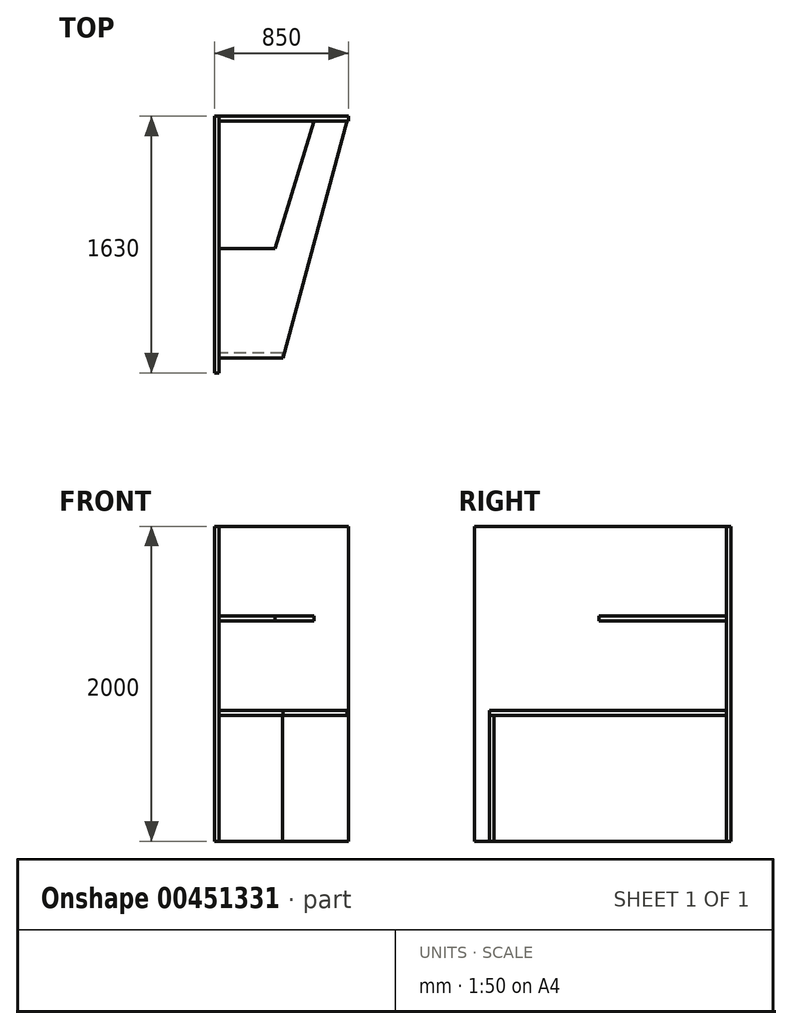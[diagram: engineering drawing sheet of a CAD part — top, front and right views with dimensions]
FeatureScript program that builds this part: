
annotation { "Feature Type Name" : "Feature", "Feature Type Description" : "" }
export const myFeature = defineFeature(function(context is Context, id is Id, definition is map)
    precondition{}
    {
        {
            var Q0;
            Q0=qCreatedBy(makeId("Top.planeOp"),FACE);
            var sketch = newSketch(context, id + "F0", { "sketchPlane" : qUnion([Q0])});
            skLineSegment(sketch, "E0.bottom", {"start": v(0, 0) * mm, "end": v(820, 0) * mm});
            skLineSegment(sketch, "E0.top", {"start": v(0, -30) * mm, "end": v(820, -30) * mm});
            skLineSegment(sketch, "E0.left", {"start": v(0, 0) * mm, "end": v(0, -30) * mm});
            skLineSegment(sketch, "E0.right", {"start": v(820, 0) * mm, "end": v(820, -30) * mm});
            skLineSegment(sketch, "E1.bottom", {"start": v(0, 0) * mm, "end": v(-30, 0) * mm});
            skLineSegment(sketch, "E1.top", {"start": v(0, -1630) * mm, "end": v(-30, -1630) * mm});
            skLineSegment(sketch, "E1.left", {"start": v(0, 0) * mm, "end": v(0, -1630) * mm});
            skLineSegment(sketch, "E1.right", {"start": v(-30, 0) * mm, "end": v(-30, -1630) * mm});
            skSolve(sketch);
        }
        {
            var Q0;
            Q0 = qSketchRegion(id + "F0", true);
            extrude(context, id + "F1", {"entities" : qUnion([Q0]), "depth" : 2000 * mm});
        }
        {
            var Q0;
            Q0=qCreatedBy(makeId("Top.planeOp"),FACE);
            cPlane(context, id + "F2", {"entities" : qUnion([Q0]), "cplaneType" : CPlaneType.OFFSET, "offset" : 800 * mm, "width" : 150 * mm, "height" : 150 * mm});
        }
        {
            var Q0;
            Q0=qCreatedBy(id+"F2.planeOp",FACE);
            var sketch = newSketch(context, id + "F3", { "sketchPlane" : qUnion([Q0])});
            skLineSegment(sketch, "E2", {"start": v(0, -30) * mm, "end": v(810, -30) * mm});
            skLineSegment(sketch, "E3", {"start": v(810, -30) * mm, "end": v(405, -1535) * mm});
            skLineSegment(sketch, "E4", {"start": v(405, -1535) * mm, "end": v(0, -1535) * mm});
            skLineSegment(sketch, "E5", {"start": v(0, -1535) * mm, "end": v(0, -30) * mm});
            skSolve(sketch);
        }
        {
            var Q0;
            Q0=qCreatedBy(makeId("Top.planeOp"),FACE);
            var sketch = newSketch(context, id + "F4", { "sketchPlane" : qUnion([Q0])});
            skSolve(sketch);
        }
        {
            var Q0;
            Q0 = qSketchRegion(id + "F3", true);
            extrude(context, id + "F5", {"entities" : qUnion([Q0]), "depth" : 30 * mm});
        }
        {
            var Q0;
            Q0=qCreatedBy(makeId("Top.planeOp"),FACE);
            cPlane(context, id + "F6", {"entities" : qUnion([Q0]), "cplaneType" : CPlaneType.OFFSET, "offset" : 1400 * mm, "width" : 150 * mm, "height" : 150 * mm});
        }
        {
            var Q0;
            Q0=qCreatedBy(id+"F6.planeOp",FACE);
            var sketch = newSketch(context, id + "F7", { "sketchPlane" : qUnion([Q0])});
            skLineSegment(sketch, "E6", {"start": v(0, -840) * mm, "end": v(355, -840) * mm});
            skLineSegment(sketch, "E7", {"start": v(355, -840) * mm, "end": v(600, -30) * mm});
            skLineSegment(sketch, "E8", {"start": v(600, -30) * mm, "end": v(0, -30) * mm});
            skLineSegment(sketch, "E9", {"start": v(0, -30) * mm, "end": v(0, -840) * mm});
            skSolve(sketch);
        }
        {
            var Q0;
            Q0 = qSketchRegion(id + "F7", true);
            extrude(context, id + "F8", {"entities" : qUnion([Q0]), "operationType" : NewBodyOperationType.ADD, "depth" : 30 * mm});
        }
        {
            var Q0;
            Q0=makeQuery(id+"F1.opExtrude","CAP_FACE",FACE,{"disambiguationData":[OSD([sQuery(id+"F0.wireOp",EDGE,"E1.bottom"),sQuery(id+"F0.wireOp",EDGE,"E1.top"),sQuery(id+"F0.wireOp",EDGE,"E1.left"),sQuery(id+"F0.wireOp",EDGE,"E1.right")])],"isStart":true});
            var sketch = newSketch(context, id + "F9", { "sketchPlane" : qUnion([Q0])});
            skLineSegment(sketch, "E10.bottom", {"start": v(400, 1535) * mm, "end": v(0, 1535) * mm});
            skLineSegment(sketch, "E10.top", {"start": v(400, 1505) * mm, "end": v(0, 1505) * mm});
            skLineSegment(sketch, "E10.left", {"start": v(0, 1535) * mm, "end": v(0, 1505) * mm});
            skLineSegment(sketch, "E10.right", {"start": v(400, 1535) * mm, "end": v(400, 1505) * mm});
            skSolve(sketch);
        }
        {
            var Q0;
            Q0 = qSketchRegion(id + "F9", true);
            var Q1;
            Q1=makeQuery(id+"F5.opExtrude","CAP_FACE",FACE,{"disambiguationData":[OSD([sQuery(id+"F3.wireOp",EDGE,"E2"),sQuery(id+"F3.wireOp",EDGE,"E3"),sQuery(id+"F3.wireOp",EDGE,"E4"),sQuery(id+"F3.wireOp",EDGE,"E5")])],"isStart":true});
            extrude(context, id + "F10", {"entities" : qUnion([Q0]), "endBound" : BoundingType.UP_TO_SURFACE, "oppositeDirection" : true, "endBoundEntityFace" : qUnion([Q1]), "depth" : 25 * mm});
        }
    });
